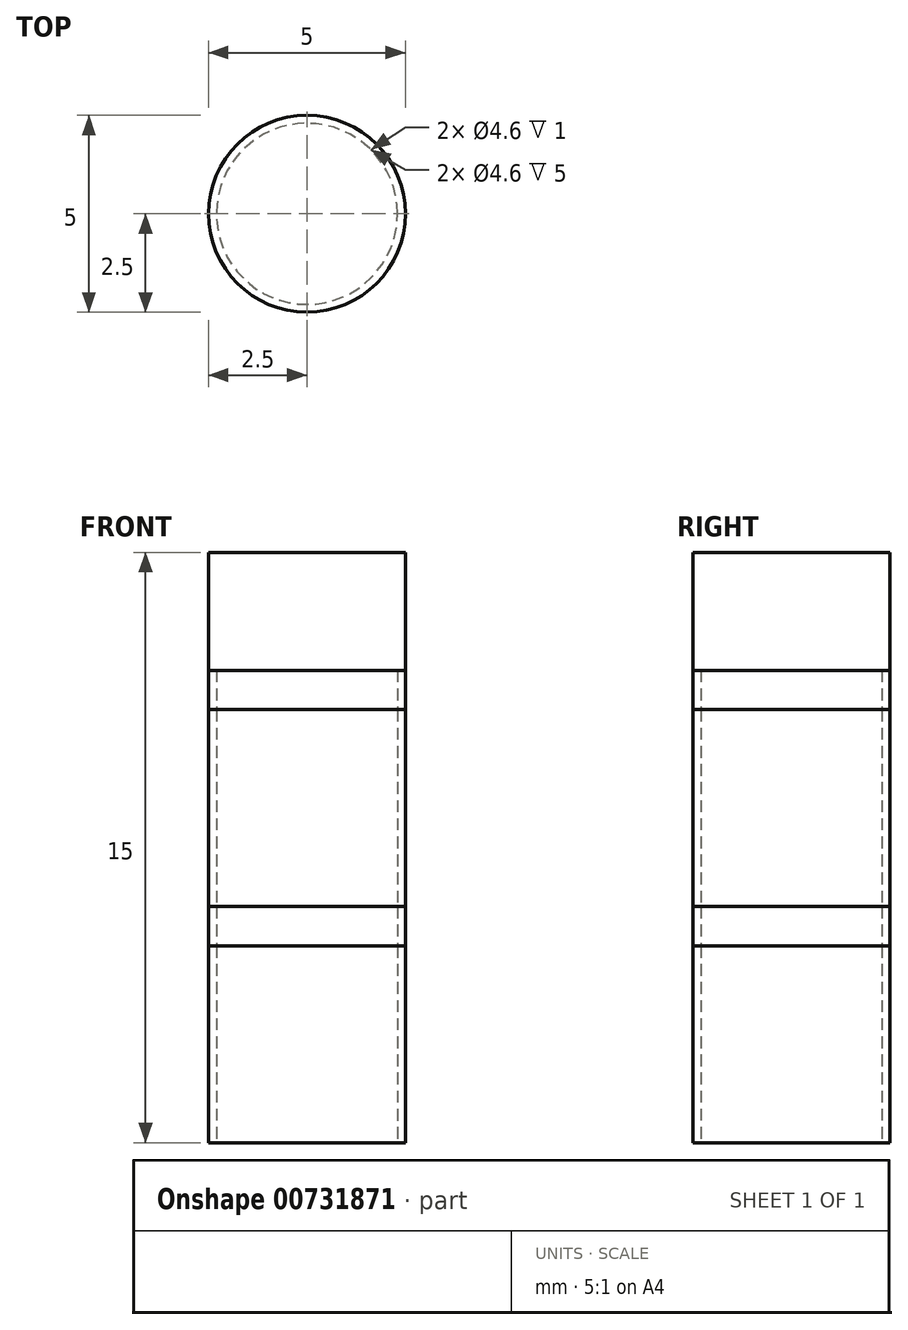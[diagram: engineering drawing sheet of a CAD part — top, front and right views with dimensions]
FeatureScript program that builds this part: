
annotation { "Feature Type Name" : "Feature", "Feature Type Description" : "" }
export const myFeature = defineFeature(function(context is Context, id is Id, definition is map)
    precondition{}
    {
        {
            var Q0;
            Q0=qCreatedBy(makeId("Top.planeOp"),FACE);
            var sketch = newSketch(context, id + "F0", { "sketchPlane" : qUnion([Q0])});
            skCircle(sketch, "E0", {"center": v(0, 0) * mm, "radius": 2.5 * mm});
            skCircle(sketch, "E1", {"center": v(0, 0) * mm, "radius": 2.4 * mm});
            skSolve(sketch);
        }
        {
            var Q0;
            Q0=makeQuery(id+"F0.imprint","IMPRINT",FACE,{"disambiguationData":[TD([[makeQuery(id+"F0.imprint","IMPRINT",EDGE,{"derivedFrom":sQuery(id+"F0.wireOp",EDGE,"E0")}),1.0]])]});
            var Q1;
            Q1=makeQuery(id+"F0.imprint","IMPRINT",FACE,{"disambiguationData":[TD([[makeQuery(id+"F0.imprint","IMPRINT",EDGE,{"derivedFrom":sQuery(id+"F0.wireOp",EDGE,"E1")}),1.0]])]});
            extrude(context, id + "F1", {"entities" : qUnion([Q0, Q1]), "depth" : 5 * mm, "offsetDistance" : 25.4 * mm});
        }
        {
            var Q0;
            Q0=makeQuery(id+"F1.opExtrude","CAP_FACE",FACE,{"disambiguationData":[OSD([sQuery(id+"F0.wireOp",EDGE,"E0")])],"isStart":false});
            extrude(context, id + "F2", {"entities" : qUnion([Q0]), "depth" : 1 * mm, "offsetDistance" : 25.4 * mm});
        }
        {
            var Q0;
            Q0=makeQuery(id+"F2.opExtrude","CAP_FACE",FACE,{"disambiguationData":[OSD([sQuery(id+"F0.wireOp",EDGE,"E0")])],"isStart":false});
            extrude(context, id + "F3", {"entities" : qUnion([Q0]), "depth" : 5 * mm, "offsetDistance" : 25.4 * mm});
        }
        {
            var Q0;
            Q0=makeQuery(id+"F3.opExtrude","CAP_FACE",FACE,{"disambiguationData":[OSD([sQuery(id+"F0.wireOp",EDGE,"E0")])],"isStart":false});
            extrude(context, id + "F4", {"entities" : qUnion([Q0]), "depth" : 1 * mm, "offsetDistance" : 25.4 * mm});
        }
        {
            var Q0;
            Q0=makeQuery(id+"F4.opExtrude","CAP_FACE",FACE,{"disambiguationData":[OSD([sQuery(id+"F0.wireOp",EDGE,"E0")])],"isStart":false});
            extrude(context, id + "F5", {"entities" : qUnion([Q0]), "depth" : 3 * mm, "offsetDistance" : 25.4 * mm});
        }
        {
            var Q0;
            Q0=makeQuery(id+"F1.opExtrude","CAP_FACE",FACE,{"disambiguationData":[OSD([sQuery(id+"F0.wireOp",EDGE,"E0")])],"isStart":true});
            var Q1;
            Q1=makeQuery(id+"F2.opExtrude","CAP_FACE",FACE,{"disambiguationData":[OSD([sQuery(id+"F0.wireOp",EDGE,"E0")])],"isStart":true});
            var Q2;
            Q2=makeQuery(id+"F4.opExtrude","CAP_FACE",FACE,{"disambiguationData":[OSD([sQuery(id+"F0.wireOp",EDGE,"E0")])],"isStart":true});
            var Q3;
            Q3=makeQuery(id+"F2.opExtrude","CAP_FACE",FACE,{"disambiguationData":[OSD([sQuery(id+"F0.wireOp",EDGE,"E0")])],"isStart":false});
            var Q4;
            Q4=makeQuery(id+"F1.opExtrude","CAP_FACE",FACE,{"disambiguationData":[OSD([sQuery(id+"F0.wireOp",EDGE,"E0")])],"isStart":false});
            var Q5;
            Q5=makeQuery(id+"F4.opExtrude","CAP_FACE",FACE,{"disambiguationData":[OSD([sQuery(id+"F0.wireOp",EDGE,"E0")])],"isStart":false});
            var Q6;
            Q6=makeQuery(id+"F3.opExtrude","CAP_FACE",FACE,{"disambiguationData":[OSD([sQuery(id+"F0.wireOp",EDGE,"E0")])],"isStart":false});
            var Q7;
            Q7=makeQuery(id+"F3.opExtrude","CAP_FACE",FACE,{"disambiguationData":[OSD([sQuery(id+"F0.wireOp",EDGE,"E0")])],"isStart":true});
            shell(context, id + "F6", {"entities" : qUnion([Q0, Q1, Q2, Q3, Q4, Q5, Q6, Q7]), "thickness" : 0.2 * mm});
        }
    });
